# Revit family: LHBG24
name_source: partatom
category: Lighting Fixtures
units: mm (PartAtom-declared; Revit-internal decimal feet)

## family parameters
Always vertical = Yes
Cut with Voids When Loaded = No
Host = Ceiling
Light Source = Yes
OmniClass Number = 23.80.70.11.14.11
OmniClass Title = Downlights
Part Type = Normal
Room Calculation Point = No
Round Connector Dimension = Use Diameter
Shared = No

## types (2) — shared parameters
Assembly Code = D5020200
Color Filter = 16777215
Description = LED High Bay G
Dimming Lamp Color Temperature Shift = <None>
Emit Shape Visible in Rendering = No
Emit from Rectangle Length = 2' - 0"
Emit from Rectangle Width = 1' - 4"
Height = 0' - 3 1/2"
Housing Finish = Metal - Viscor - White
Lamp = LED
Length = 2' - 0"
Lens Finish = Acrylic - Viscor - Frosted, Impact Round Extruded
Louver Finish = Metal - Viscor - White Gloss F06
Manufacturer = VISIONEERING by VISCOR
Model = LHBG
Tilt Angle = 90.00°
URL = https://www.viscor.com
Voltage = 120 V
Width = 1' - 4"

## per-type parameters (varying)
| type | Apparent Load | Lamp Wattage | Photometric Web File |
| LHBG24-LED840K090LUNV-P73W1 | 67 VA | 67 VA | LHBG24-LED840K090LUNV-P73W1.ies |
| LHBG24-LED840K120LUNV-P73W1 | 103 VA | 103 VA | LHBG24-LED840K120LUNV-P73W1.IES |

## geometry (parser evidence)
native form markers: Sweep x3
no freeform markers — native parametric forms only
